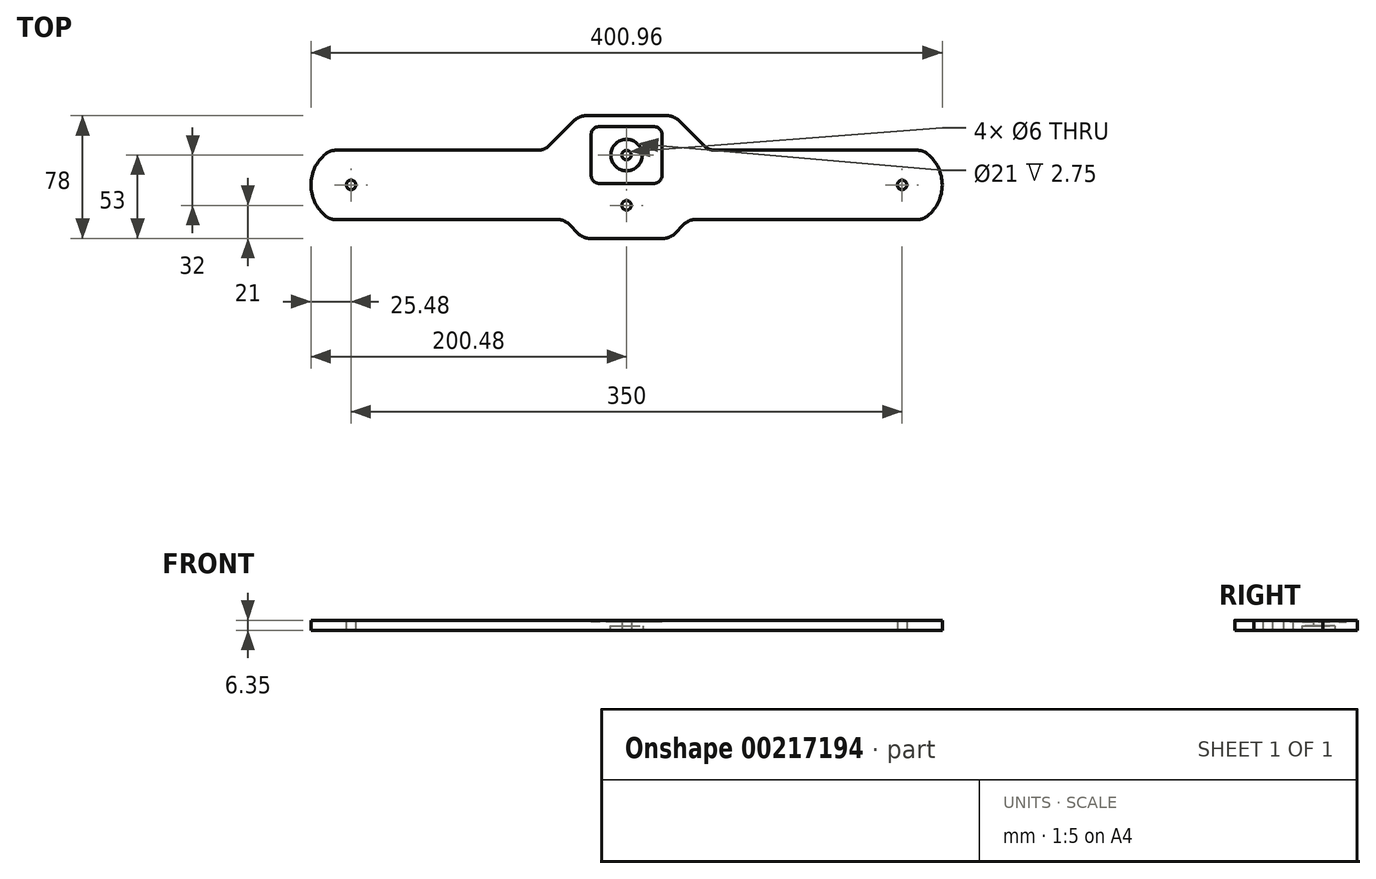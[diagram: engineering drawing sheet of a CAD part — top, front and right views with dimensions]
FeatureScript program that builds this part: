
annotation { "Feature Type Name" : "Feature", "Feature Type Description" : "" }
export const myFeature = defineFeature(function(context is Context, id is Id, definition is map)
    precondition{}
    {
        {
            var Q0;
            Q0=qCreatedBy(makeId("Top.planeOp"),FACE);
            var sketch = newSketch(context, id + "F0", { "sketchPlane" : qUnion([Q0])});
            skCircle(sketch, "E0", {"center": v(0, 19) * mm, "radius": 3 * mm});
            skLineSegment(sketch, "E1", {"start": v(0, 44) * mm, "end": v(-25.86, 44) * mm});
            skLineSegment(sketch, "E2", {"start": v(-32.93, 41.07) * mm, "end": v(-49.07, 24.93) * mm});
            skLineSegment(sketch, "E3", {"start": v(-56.14, 22) * mm, "end": v(-187.85, 22) * mm});
            skLineSegment(sketch, "E4", {"start": v(-187.85, -22) * mm, "end": v(-43.64, -22) * mm});
            skArc(sketch, "E5", {"start": v(-187.85, 22) * mm, "mid": v(-200.48, 0) * mm, "end": v(-187.85, -22) * mm});
            skLineSegment(sketch, "E6.MirrorCS", {"start": v(0, 44) * mm, "end": v(25.86, 44) * mm});
            skLineSegment(sketch, "E7.MirrorCS", {"start": v(32.93, 41.07) * mm, "end": v(49.07, 24.93) * mm});
            skLineSegment(sketch, "E8.MirrorCS", {"start": v(56.14, 22) * mm, "end": v(187.85, 22) * mm});
            skArc(sketch, "E9.MirrorCS", {"start": v(187.85, 22) * mm, "mid": v(200.48, 0) * mm, "end": v(187.85, -22) * mm});
            skLineSegment(sketch, "E10.MirrorCS", {"start": v(187.85, -22) * mm, "end": v(43.64, -22) * mm});
            skPoint(sketch, "E11.visualSharp", {"position": v(-52, 22) * mm});
            skArc(sketch, "E11.filletArc", {"start": v(-56.14, 22) * mm, "mid": v(-52.32, 22.76) * mm, "end": v(-49.07, 24.93) * mm});
            skPoint(sketch, "E12.visualSharp", {"position": v(-30, 44) * mm});
            skArc(sketch, "E12.filletArc", {"start": v(-25.86, 44) * mm, "mid": v(-29.68, 43.24) * mm, "end": v(-32.93, 41.07) * mm});
            skPoint(sketch, "E13.visualSharp", {"position": v(30, 44) * mm});
            skArc(sketch, "E13.filletArc", {"start": v(32.93, 41.07) * mm, "mid": v(29.68, 43.24) * mm, "end": v(25.86, 44) * mm});
            skPoint(sketch, "E14.visualSharp", {"position": v(52, 22) * mm});
            skArc(sketch, "E14.filletArc", {"start": v(49.07, 24.93) * mm, "mid": v(52.32, 22.76) * mm, "end": v(56.14, 22) * mm});
            skCircle(sketch, "E15", {"center": v(-175, 0) * mm, "radius": 3 * mm});
            skCircle(sketch, "E16.MirrorC", {"center": v(175, 0) * mm, "radius": 3 * mm});
            skLineSegment(sketch, "E17", {"start": v(-36.57, -24.93) * mm, "end": v(-30.43, -31.07) * mm});
            skLineSegment(sketch, "E18", {"start": v(-23.36, -34) * mm, "end": v(0, -34) * mm});
            skLineSegment(sketch, "E19.MirrorCS", {"start": v(23.36, -34) * mm, "end": v(0, -34) * mm});
            skLineSegment(sketch, "E20.MirrorCS", {"start": v(36.57, -24.93) * mm, "end": v(30.43, -31.07) * mm});
            skPoint(sketch, "E21.orphan", {"position": v(0, -22) * mm});
            skPoint(sketch, "E22.visualSharp", {"position": v(-39.5, -22) * mm});
            skArc(sketch, "E22.filletArc", {"start": v(-36.57, -24.93) * mm, "mid": v(-39.82, -22.76) * mm, "end": v(-43.64, -22) * mm});
            skPoint(sketch, "E23.visualSharp", {"position": v(-27.5, -34) * mm});
            skArc(sketch, "E23.filletArc", {"start": v(-30.43, -31.07) * mm, "mid": v(-27.18, -33.24) * mm, "end": v(-23.36, -34) * mm});
            skPoint(sketch, "E24.visualSharp", {"position": v(27.5, -34) * mm});
            skArc(sketch, "E24.filletArc", {"start": v(23.36, -34) * mm, "mid": v(27.18, -33.24) * mm, "end": v(30.43, -31.07) * mm});
            skPoint(sketch, "E25.visualSharp", {"position": v(39.5, -22) * mm});
            skArc(sketch, "E25.filletArc", {"start": v(43.64, -22) * mm, "mid": v(39.82, -22.76) * mm, "end": v(36.57, -24.93) * mm});
            skCircle(sketch, "E26", {"center": v(0, -13) * mm, "radius": 3 * mm});
            skSolve(sketch);
        }
        {
            var Q0;
            Q0=makeQuery(id+"F0.imprint","IMPRINT",FACE,{"disambiguationData":[TD([[makeQuery(id+"F0.imprint","IMPRINT",EDGE,{"derivedFrom":sQuery(id+"F0.wireOp",EDGE,"anvxqUEY-zb5h-UAzJ-OBB1-QoTpabNhaUVH")}),-1.0]])]});
            var Q1;
            Q1=makeQuery(id+"F0.imprint","IMPRINT",FACE,{"disambiguationData":[TD([[makeQuery(id+"F0.imprint","IMPRINT",EDGE,{"derivedFrom":sQuery(id+"F0.wireOp",EDGE,"E0")}),-1.0]])]});
            extrude(context, id + "F1", {"entities" : qUnion([Q0, Q1]), "depth" : 6.35 * mm});
        }
        {
            var Q0;
            Q0=makeQuery(id+"F1.opExtrude","SWEPT_EDGE",EDGE,{"disambiguationData":[OSD([sQuery(id+"F0.wireOp",EDGE,"E3"),sQuery(id+"F0.wireOp",EDGE,"E5")])]});
            var Q1;
            Q1=makeQuery(id+"F1.opExtrude","SWEPT_EDGE",EDGE,{"disambiguationData":[OSD([sQuery(id+"F0.wireOp",EDGE,"E4"),sQuery(id+"F0.wireOp",EDGE,"E5")])]});
            var Q2;
            Q2=makeQuery(id+"F1.opExtrude","SWEPT_EDGE",EDGE,{"disambiguationData":[OSD([sQuery(id+"F0.wireOp",EDGE,"E9.MirrorCS"),sQuery(id+"F0.wireOp",EDGE,"E10.MirrorCS")])]});
            var Q3;
            Q3=makeQuery(id+"F1.opExtrude","SWEPT_EDGE",EDGE,{"disambiguationData":[OSD([sQuery(id+"F0.wireOp",EDGE,"E8.MirrorCS"),sQuery(id+"F0.wireOp",EDGE,"E9.MirrorCS")])]});
            fillet(context, id + "F2", {"entities" : qUnion([Q0, Q1, Q2, Q3]), "radius" : 10 * mm, "tangentPropagation" : true, "allowEdgeOverflow" : false});
        }
        {
            var Q0;
            Q0=makeQuery(id+"F1.opExtrude","CAP_FACE",FACE,{"disambiguationData":[OSD([sQuery(id+"F0.wireOp",EDGE,"E0"),sQuery(id+"F0.wireOp",EDGE,"E1"),sQuery(id+"F0.wireOp",EDGE,"E2"),sQuery(id+"F0.wireOp",EDGE,"E3"),sQuery(id+"F0.wireOp",EDGE,"E4"),sQuery(id+"F0.wireOp",EDGE,"E5"),sQuery(id+"F0.wireOp",EDGE,"E6.MirrorCS"),sQuery(id+"F0.wireOp",EDGE,"E7.MirrorCS"),sQuery(id+"F0.wireOp",EDGE,"E8.MirrorCS"),sQuery(id+"F0.wireOp",EDGE,"E9.MirrorCS"),sQuery(id+"F0.wireOp",EDGE,"E10.MirrorCS"),sQuery(id+"F0.wireOp",EDGE,"E11.filletArc"),sQuery(id+"F0.wireOp",EDGE,"E12.filletArc"),sQuery(id+"F0.wireOp",EDGE,"E13.filletArc"),sQuery(id+"F0.wireOp",EDGE,"E14.filletArc"),sQuery(id+"F0.wireOp",EDGE,"E15"),sQuery(id+"F0.wireOp",EDGE,"E16.MirrorC"),sQuery(id+"F0.wireOp",EDGE,"E17"),sQuery(id+"F0.wireOp",EDGE,"E18"),sQuery(id+"F0.wireOp",EDGE,"E19.MirrorCS"),sQuery(id+"F0.wireOp",EDGE,"E20.MirrorCS"),sQuery(id+"F0.wireOp",EDGE,"E22.filletArc"),sQuery(id+"F0.wireOp",EDGE,"E23.filletArc"),sQuery(id+"F0.wireOp",EDGE,"E24.filletArc"),sQuery(id+"F0.wireOp",EDGE,"E25.filletArc"),sQuery(id+"F0.wireOp",EDGE,"E26")])],"isStart":true});
            var sketch = newSketch(context, id + "F3", { "sketchPlane" : qUnion([Q0])});
            skCircle(sketch, "E27", {"center": v(0, -19) * mm, "radius": 10.5 * mm});
            skSolve(sketch);
        }
        {
            var Q0;
            Q0 = qSketchRegion(id + "F3", true);
            extrude(context, id + "F4", {"entities" : qUnion([Q0]), "operationType" : NewBodyOperationType.REMOVE, "oppositeDirection" : true, "depth" : 2.75 * mm});
        }
        {
            var Q0;
            Q0=makeQuery(id+"F1.opExtrude","CAP_FACE",FACE,{"disambiguationData":[OSD([sQuery(id+"F0.wireOp",EDGE,"E0"),sQuery(id+"F0.wireOp",EDGE,"E1"),sQuery(id+"F0.wireOp",EDGE,"E2"),sQuery(id+"F0.wireOp",EDGE,"E3"),sQuery(id+"F0.wireOp",EDGE,"E4"),sQuery(id+"F0.wireOp",EDGE,"E5"),sQuery(id+"F0.wireOp",EDGE,"E6.MirrorCS"),sQuery(id+"F0.wireOp",EDGE,"E7.MirrorCS"),sQuery(id+"F0.wireOp",EDGE,"E8.MirrorCS"),sQuery(id+"F0.wireOp",EDGE,"E9.MirrorCS"),sQuery(id+"F0.wireOp",EDGE,"E10.MirrorCS"),sQuery(id+"F0.wireOp",EDGE,"E11.filletArc"),sQuery(id+"F0.wireOp",EDGE,"E12.filletArc"),sQuery(id+"F0.wireOp",EDGE,"E13.filletArc"),sQuery(id+"F0.wireOp",EDGE,"E14.filletArc"),sQuery(id+"F0.wireOp",EDGE,"E15"),sQuery(id+"F0.wireOp",EDGE,"E16.MirrorC"),sQuery(id+"F0.wireOp",EDGE,"E17"),sQuery(id+"F0.wireOp",EDGE,"E18"),sQuery(id+"F0.wireOp",EDGE,"E19.MirrorCS"),sQuery(id+"F0.wireOp",EDGE,"E20.MirrorCS"),sQuery(id+"F0.wireOp",EDGE,"E22.filletArc"),sQuery(id+"F0.wireOp",EDGE,"E23.filletArc"),sQuery(id+"F0.wireOp",EDGE,"E24.filletArc"),sQuery(id+"F0.wireOp",EDGE,"E25.filletArc"),sQuery(id+"F0.wireOp",EDGE,"E26")])],"isStart":false});
            var sketch = newSketch(context, id + "F5", { "sketchPlane" : qUnion([Q0])});
            skLineSegment(sketch, "E28.bottom", {"start": v(17.5, 37) * mm, "end": v(-17.5, 37) * mm});
            skLineSegment(sketch, "E28.top", {"start": v(17.5, 1) * mm, "end": v(-17.5, 1) * mm});
            skLineSegment(sketch, "E28.left", {"start": v(22.5, 32) * mm, "end": v(22.5, 6) * mm});
            skLineSegment(sketch, "E28.right", {"start": v(-22.5, 32) * mm, "end": v(-22.5, 6) * mm});
            skPoint(sketch, "E28.middle", {"position": v(0, 19) * mm});
            skPoint(sketch, "E29.visualSharp", {"position": v(-22.5, 37) * mm});
            skArc(sketch, "E29.filletArc", {"start": v(-17.5, 37) * mm, "mid": v(-21.04, 35.54) * mm, "end": v(-22.5, 32) * mm});
            skPoint(sketch, "E30.visualSharp", {"position": v(22.5, 37) * mm});
            skArc(sketch, "E30.filletArc", {"start": v(22.5, 32) * mm, "mid": v(21.04, 35.54) * mm, "end": v(17.5, 37) * mm});
            skPoint(sketch, "E31.visualSharp", {"position": v(22.5, 1) * mm});
            skArc(sketch, "E31.filletArc", {"start": v(17.5, 1) * mm, "mid": v(21.04, 2.46) * mm, "end": v(22.5, 6) * mm});
            skPoint(sketch, "E32.visualSharp", {"position": v(-22.5, 1) * mm});
            skArc(sketch, "E32.filletArc", {"start": v(-22.5, 6) * mm, "mid": v(-21.04, 2.46) * mm, "end": v(-17.5, 1) * mm});
            skCircle(sketch, "E33", {"center": v(0, 19) * mm, "radius": 10 * mm});
            skSolve(sketch);
        }
        {
            var Q0;
            Q0 = qSketchRegion(id + "F5", true);
            extrude(context, id + "F6", {"entities" : qUnion([Q0]), "operationType" : NewBodyOperationType.REMOVE, "oppositeDirection" : true, "depth" : 1.1 * mm});
        }
    });
